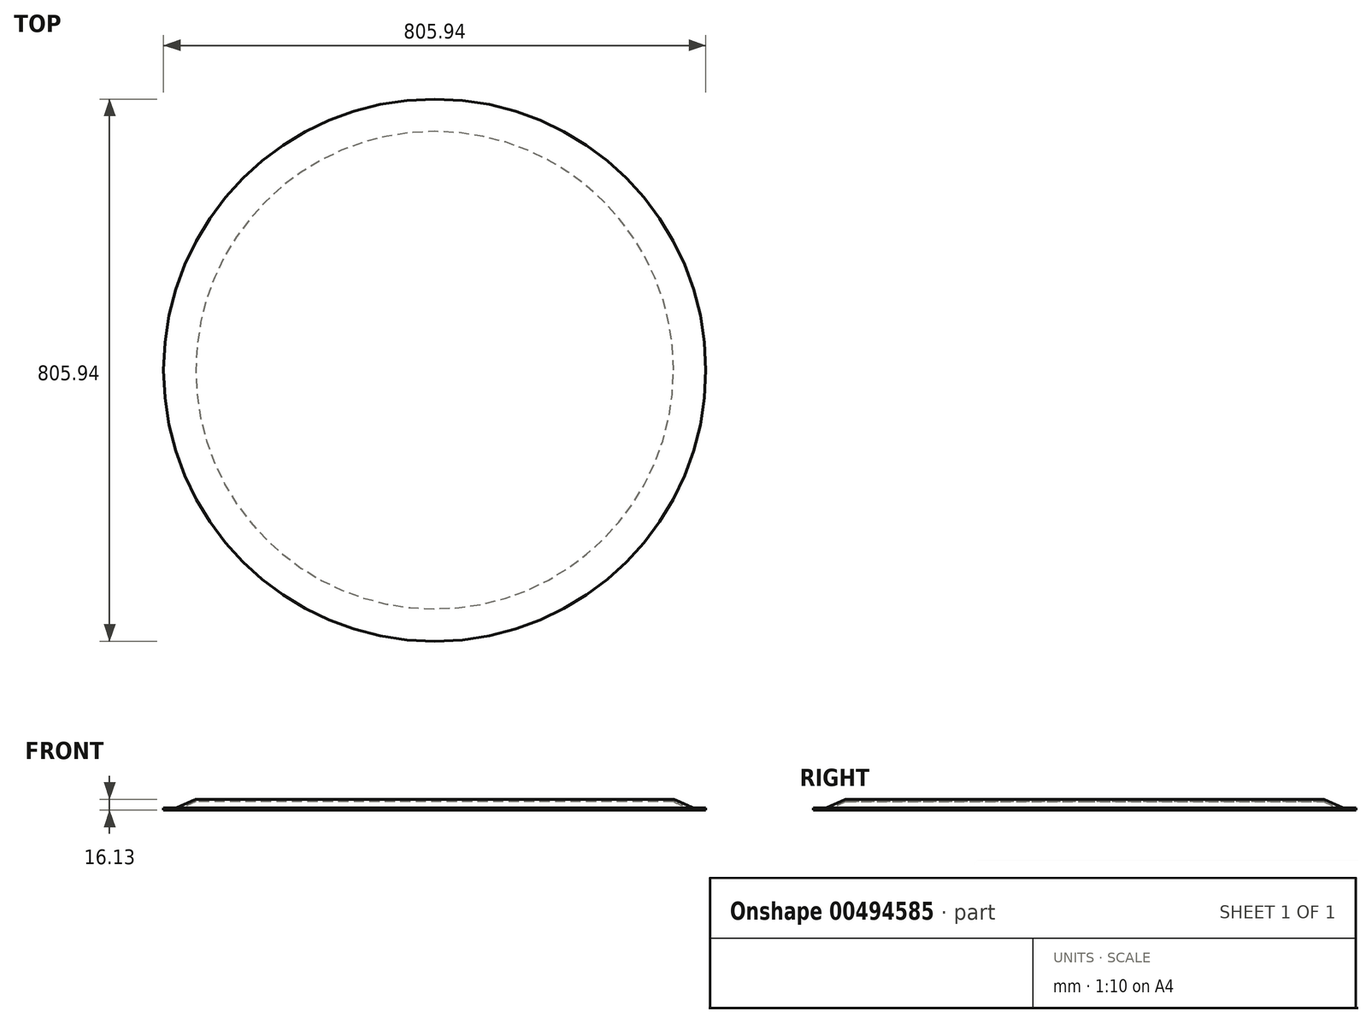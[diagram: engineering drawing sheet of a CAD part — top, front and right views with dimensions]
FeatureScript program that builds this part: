
annotation { "Feature Type Name" : "Feature", "Feature Type Description" : "" }
export const myFeature = defineFeature(function(context is Context, id is Id, definition is map)
    precondition{}
    {
        {
            var Q0;
            Q0=qCreatedBy(makeId("Front.planeOp"),FACE);
            var sketch = newSketch(context, id + "F0", { "sketchPlane" : qUnion([Q0])});
            skLineSegment(sketch, "E0", {"start": v(0, 0) * mm, "end": v(354.24, 0) * mm});
            skLineSegment(sketch, "E1", {"start": v(356.84, -0.56) * mm, "end": v(382.68, -12.14) * mm});
            skLineSegment(sketch, "E2", {"start": v(385.28, -12.7) * mm, "end": v(402.97, -12.7) * mm});
            skPoint(sketch, "E3.visualSharp", {"position": v(355.6, 0) * mm});
            skArc(sketch, "E3.filletArc", {"start": v(356.84, -0.56) * mm, "mid": v(355.57, -0.14) * mm, "end": v(354.24, 0) * mm});
            skPoint(sketch, "E4.visualSharp", {"position": v(383.92, -12.7) * mm});
            skArc(sketch, "E4.filletArc", {"start": v(382.68, -12.14) * mm, "mid": v(383.95, -12.56) * mm, "end": v(385.28, -12.7) * mm});
            skLineSegment(sketch, "E5.0", {"start": v(385.28, -16.13) * mm, "end": v(402.97, -16.13) * mm});
            skArc(sketch, "E5.1", {"start": v(381.28, -15.27) * mm, "mid": v(383.23, -15.91) * mm, "end": v(385.28, -16.13) * mm});
            skLineSegment(sketch, "E5.2", {"start": v(354.87, -3.43) * mm, "end": v(381.28, -15.27) * mm});
            skLineSegment(sketch, "E5.3", {"start": v(0, -3.43) * mm, "end": v(354.87, -3.43) * mm});
            skLineSegment(sketch, "E6", {"start": v(402.97, -12.7) * mm, "end": v(402.97, -16.13) * mm});
            skLineSegment(sketch, "E7", {"start": v(0, 0) * mm, "end": v(0, -3.43) * mm});
            skSolve(sketch);
        }
        {
            var Q0;
            Q0=makeQuery(id+"F0.imprint","IMPRINT",FACE,{"disambiguationData":[TD([[makeQuery(id+"F0.imprint","IMPRINT",EDGE,{"derivedFrom":sQuery(id+"F0.wireOp",EDGE,"E0")}),-1.0]])]});
            var Q1;
            Q1=sQuery(id+"F0.wireOp",EDGE,"E7");
            revolve(context, id + "F1", {"entities" : qUnion([Q0]), "axis" : qUnion([Q1]), "revolveType" : RevolveType.FULL});
        }
    });
